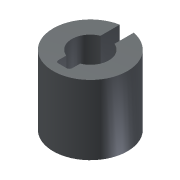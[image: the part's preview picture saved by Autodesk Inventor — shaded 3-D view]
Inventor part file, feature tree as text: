
AUTODESK INVENTOR PART (.ipt)
format: ipt  version: 2013 (Build 170138000, 138)  size: 87,040 bytes
history: native  units: in
note: dims shown in document units (in); Inventor stores cm internally (conversion verified against a paired STEP export)
features: fillet x1, other x1, imported_body x1
ambient origin geometry x8: Origin, YZ Plane, XZ Plane, XY Plane, X Axis, Y Axis, Z Axis, Center Point
feature tree (3):
  fillet  "Fillet1"  [1 undecoded]
  other  "217-2625-011 Rev11"
  imported_body  "Base1"
note: 1 required parameter value undecoded (feature->parameter linkage not recoverable at this tier; creation-order binding heuristic only, values carry confidence <= 0.55)
